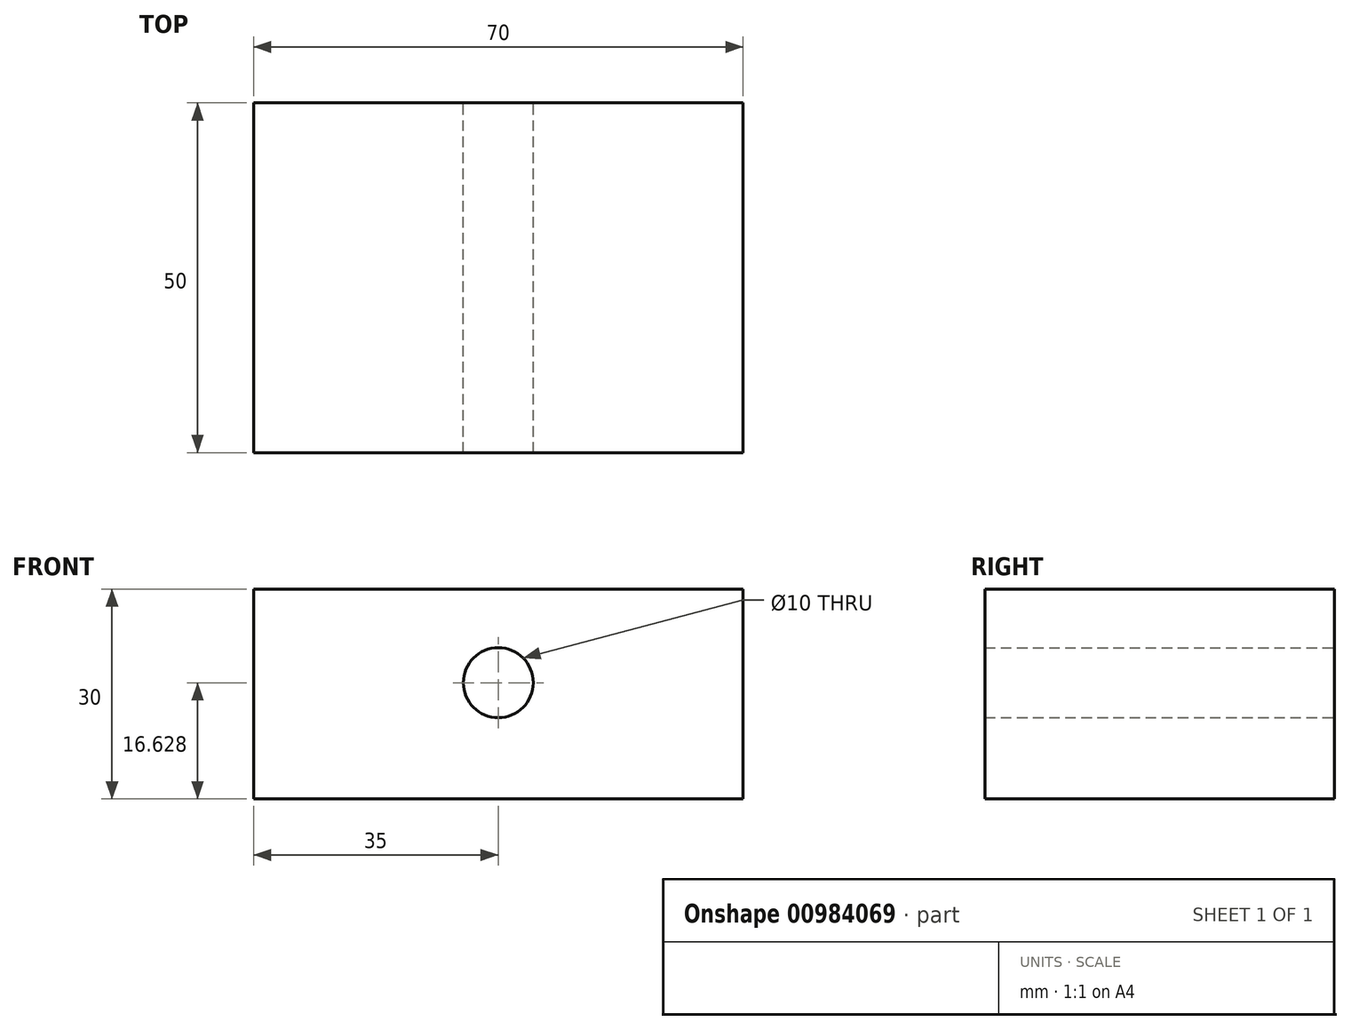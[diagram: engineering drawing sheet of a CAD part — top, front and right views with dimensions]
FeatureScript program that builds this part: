
annotation { "Feature Type Name" : "Feature", "Feature Type Description" : "" }
export const myFeature = defineFeature(function(context is Context, id is Id, definition is map)
    precondition{}
    {
        {
            var Q0;
            Q0=qCreatedBy(makeId("Front.planeOp"),FACE);
            var sketch = newSketch(context, id + "F0", { "sketchPlane" : qUnion([Q0])});
            skLineSegment(sketch, "E0.bottom", {"start": v(0, 0) * mm, "end": v(70, 0) * mm});
            skLineSegment(sketch, "E0.top", {"start": v(0, 30) * mm, "end": v(70, 30) * mm});
            skLineSegment(sketch, "E0.left", {"start": v(0, 0) * mm, "end": v(0, 30) * mm});
            skLineSegment(sketch, "E0.right", {"start": v(70, 0) * mm, "end": v(70, 30) * mm});
            skCircle(sketch, "E1", {"center": v(35, 16.63) * mm, "radius": 5 * mm});
            skLineSegment(sketch, "E2", {"start": v(35, 30) * mm, "end": v(35, 0) * mm, "construction": true});
            skSolve(sketch);
        }
        {
            var Q0;
            Q0=makeQuery(id+"F0.imprint","IMPRINT",FACE,{"disambiguationData":[TD([[makeQuery(id+"F0.imprint","IMPRINT",EDGE,{"derivedFrom":sQuery(id+"F0.wireOp",EDGE,"E0.bottom")}),1.0]])]});
            extrude(context, id + "F1", {"entities" : qUnion([Q0]), "depth" : 50 * mm, "offsetDistance" : 25 * mm});
        }
    });
